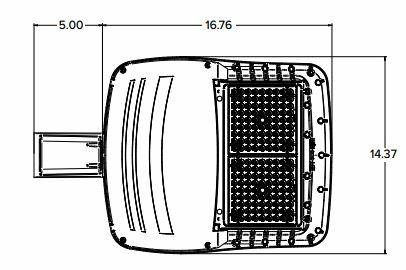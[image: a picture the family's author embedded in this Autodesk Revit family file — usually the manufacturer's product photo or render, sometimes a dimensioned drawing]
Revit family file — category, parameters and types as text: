
# Revit family: VP-1_K
name_source: partatom
category: Lighting Fixtures
units: mm (PartAtom-declared; Revit-internal decimal feet)

## family parameters
Cut with Voids When Loaded = No
Host = Face
Light Source = No
OmniClass Number = 23.80.70.11.14.17
OmniClass Title = Direct/Indirect
Part Type = Normal
Room Calculation Point = No
Round Connector Dimension = Use Diameter
Shared = Yes

## types (1)
- VP-1-K
    Apparent Load = 97 VA
    Assembly Code = D5020200
    Brand = Beacon
    CRI = 70
    Certification = UL
    Cool Grey = Cool Grey
    Default Elevation = 48 "
    Description = The Viper is an extremely versatile area/site luminaire which blends design, performance, and technology for a variety of applications.
    Features = Featuring two different optical technologies, Micro Strike and Strike Optics, which provide the best distribution patterns for retrofit or new construction
Vibration rated for high vibration applications including bridges and overpasses
Control options including photo control, occupancy sensing, NX Lighting Controls, wiSCAPE and 7-Pin with networked controls
Mounting options include: Arm, Universal Arm, Adjustable Arm, Mast Arm, Decorative Arm, Knuckle, Trunnion, Wall
Distribution options include: Auto Front Row, Type 2, Type 3, Type 4 Forward, Type 4 Wide, Type 5 Narrow, Type 5 Medium, Type 5 Wide, Type 5 Rectangular, Corner Optic, and Tennis Court
    Finish = Arctic White
    Glass = Glass
    Grey = Grey
    Lamp = LED
    Light Output = 6297 cd/m²
    Load Classification = Lighting
    Manufacturer = Current Lighting
    Matt Black = Matt Black
    Matt Grey = MATT GREY
    Matt White = Matt White
    Model = VP-1-K
    Name = Viper Area Size 1
    Power Factor = 0.9
    Product Documentation Link = https://cdn.currentlighting.com
    Product Page URL = https://www.currentlighting.com
    Type Comments = Lighting Fixture
    URL = https://www.currentlighting.com
    Voltage = 120 V
    Warranty = Five year warranty
    Wattage Comments = 97.2W

## geometry (parser evidence)
native form markers: Blend x2, Sweep x3
no freeform markers — native parametric forms only
